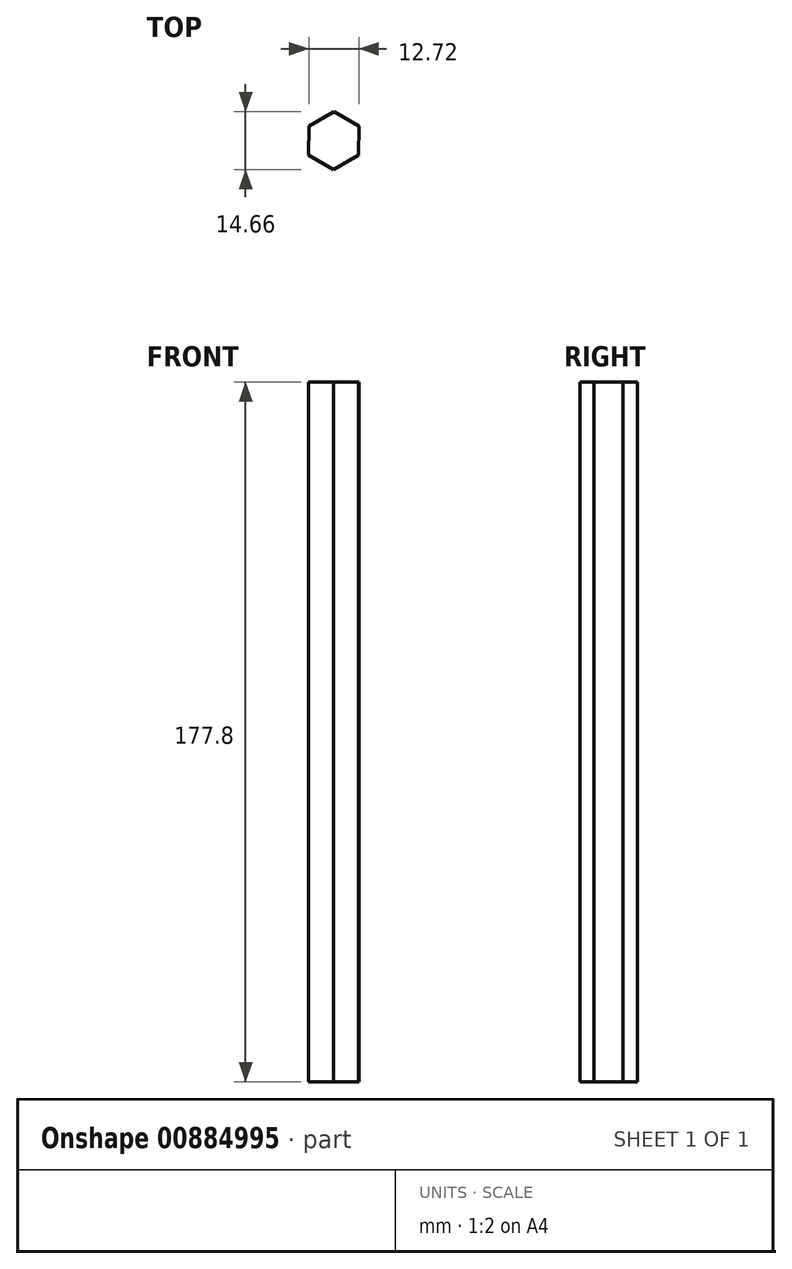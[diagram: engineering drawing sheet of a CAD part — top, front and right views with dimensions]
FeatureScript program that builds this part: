
annotation { "Feature Type Name" : "Feature", "Feature Type Description" : "" }
export const myFeature = defineFeature(function(context is Context, id is Id, definition is map)
    precondition{}
    {
        {
            var Q0;
            Q0=qCreatedBy(makeId("Top.planeOp"),FACE);
            var sketch = newSketch(context, id + "F0", { "sketchPlane" : qUnion([Q0])});
            skCircle(sketch, "E0.cCircle", {"center": v(0, 0) * mm, "radius": 6.35 * mm, "construction": true});
            skLineSegment(sketch, "E0.0", {"start": v(0.02, 7.33) * mm, "end": v(6.36, 3.64) * mm});
            skLineSegment(sketch, "E0.1", {"start": v(6.36, 3.64) * mm, "end": v(6.34, -3.69) * mm});
            skLineSegment(sketch, "E0.2", {"start": v(6.34, -3.69) * mm, "end": v(-0.02, -7.33) * mm});
            skLineSegment(sketch, "E0.3", {"start": v(-0.02, -7.33) * mm, "end": v(-6.36, -3.64) * mm});
            skLineSegment(sketch, "E0.4", {"start": v(-6.36, -3.64) * mm, "end": v(-6.34, 3.69) * mm});
            skLineSegment(sketch, "E0.5", {"start": v(-6.34, 3.69) * mm, "end": v(0.02, 7.33) * mm});
            skPoint(sketch, "E0.0.midPoint", {"position": v(3.2, 5.49) * mm});
            skSolve(sketch);
        }
        {
            var Q0;
            Q0 = qSketchRegion(id + "F0", true);
            extrude(context, id + "F1", {"entities" : qUnion([Q0]), "depth" : 177.8 * mm, "offsetDistance" : 25.4 * mm});
        }
    });
